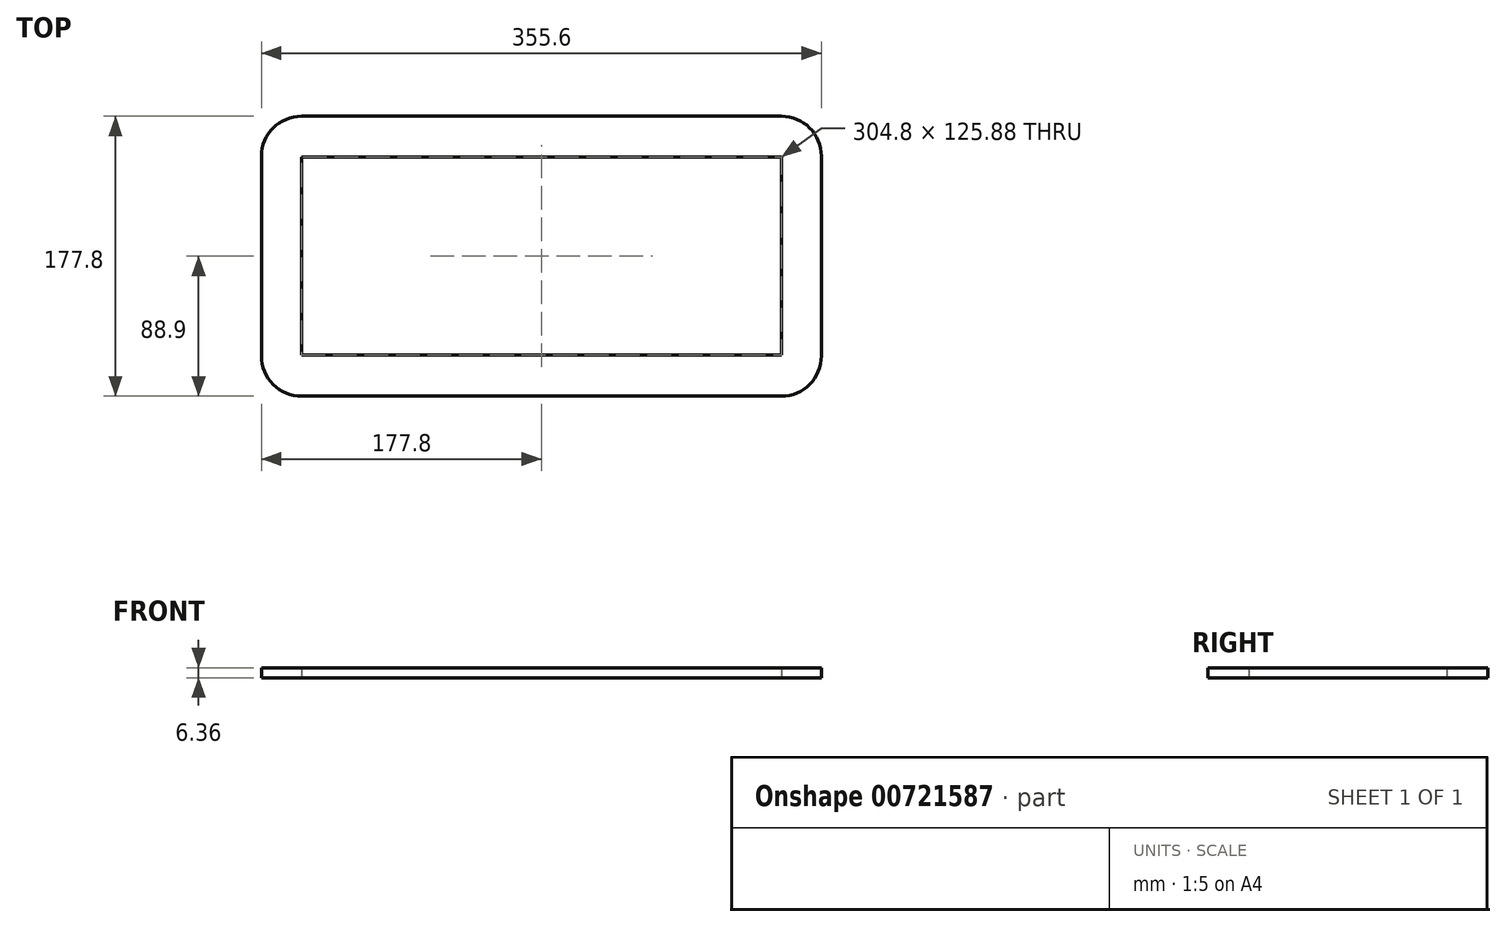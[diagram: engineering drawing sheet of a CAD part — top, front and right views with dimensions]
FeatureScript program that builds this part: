
annotation { "Feature Type Name" : "Feature", "Feature Type Description" : "" }
export const myFeature = defineFeature(function(context is Context, id is Id, definition is map)
    precondition{}
    {
        {
            var Q0;
            Q0=qCreatedBy(makeId("Top.planeOp"),FACE);
            var sketch = newSketch(context, id + "F0", { "sketchPlane" : qUnion([Q0])});
            skLineSegment(sketch, "E0.bottom", {"start": v(152.4, -62.94) * mm, "end": v(-152.4, -62.94) * mm});
            skLineSegment(sketch, "E0.top", {"start": v(152.4, 62.94) * mm, "end": v(-152.4, 62.94) * mm});
            skLineSegment(sketch, "E0.left", {"start": v(152.4, -62.94) * mm, "end": v(152.4, 62.94) * mm});
            skLineSegment(sketch, "E0.right", {"start": v(-152.4, -62.94) * mm, "end": v(-152.4, 62.94) * mm});
            skPoint(sketch, "E0.middle", {"position": v(0, 0) * mm});
            skSolve(sketch);
        }
        {
            var Q0;
            Q0=makeQuery(id+"F0.imprint","IMPRINT",FACE,{"disambiguationData":[TD([[makeQuery(id+"F0.imprint","IMPRINT",EDGE,{"derivedFrom":sQuery(id+"F0.wireOp",EDGE,"E0.bottom")}),-1.0]])]});
            extrude(context, id + "F1", {"entities" : qUnion([Q0]), "depth" : 6.35 * mm, "offsetDistance" : 25.4 * mm, "symmetric" : true});
        }
        {
            var Q0;
            Q0=qCreatedBy(makeId("Top.planeOp"),FACE);
            var sketch = newSketch(context, id + "F2", { "sketchPlane" : qUnion([Q0])});
            skLineSegment(sketch, "E1.bottom", {"start": v(177.8, -88.9) * mm, "end": v(-177.8, -88.9) * mm});
            skLineSegment(sketch, "E1.top", {"start": v(177.8, 88.9) * mm, "end": v(-177.8, 88.9) * mm});
            skLineSegment(sketch, "E1.left", {"start": v(177.8, -88.9) * mm, "end": v(177.8, 88.9) * mm});
            skLineSegment(sketch, "E1.right", {"start": v(-177.8, -88.9) * mm, "end": v(-177.8, 88.9) * mm});
            skPoint(sketch, "E1.middle", {"position": v(0, 0) * mm});
            skSolve(sketch);
        }
        {
            var Q0;
            Q0 = qSketchRegion(id + "F2", true);
            extrude(context, id + "F3", {"entities" : qUnion([Q0]), "operationType" : NewBodyOperationType.ADD, "depth" : 6.35 * mm, "offsetDistance" : 25.4 * mm, "symmetric" : true});
        }
        {
            var Q0;
            Q0 = qSketchRegion(id + "F0", true);
            extrude(context, id + "F4", {"entities" : qUnion([Q0]), "operationType" : NewBodyOperationType.REMOVE, "depth" : 25.4 * mm, "offsetDistance" : 25.4 * mm, "symmetric" : true});
        }
        {
            var Q0;
            Q0=makeQuery(id+"F3.opExtrude","SWEPT_EDGE",EDGE,{"disambiguationData":[OSD([sQuery(id+"F2.wireOp",EDGE,"E1.top"),sQuery(id+"F2.wireOp",EDGE,"E1.right")])]});
            fillet(context, id + "F5", {"entities" : qUnion([Q0]), "radius" : 25.4 * mm, "tangentPropagation" : true, "allowEdgeOverflow" : false});
        }
        {
            var Q0;
            Q0=makeQuery(id+"F3.opExtrude","SWEPT_EDGE",EDGE,{"disambiguationData":[OSD([sQuery(id+"F2.wireOp",EDGE,"E1.top"),sQuery(id+"F2.wireOp",EDGE,"E1.left")])]});
            fillet(context, id + "F6", {"entities" : qUnion([Q0]), "radius" : 25.4 * mm, "tangentPropagation" : true, "allowEdgeOverflow" : false});
        }
        {
            var Q0;
            Q0=makeQuery(id+"F3.opExtrude","SWEPT_EDGE",EDGE,{"disambiguationData":[OSD([sQuery(id+"F2.wireOp",EDGE,"E1.bottom"),sQuery(id+"F2.wireOp",EDGE,"E1.left")])]});
            fillet(context, id + "F7", {"entities" : qUnion([Q0]), "radius" : 25.4 * mm, "tangentPropagation" : true, "allowEdgeOverflow" : false});
        }
        {
            var Q0;
            Q0=makeQuery(id+"F3.opExtrude","SWEPT_EDGE",EDGE,{"disambiguationData":[OSD([sQuery(id+"F2.wireOp",EDGE,"E1.bottom"),sQuery(id+"F2.wireOp",EDGE,"E1.right")])]});
            fillet(context, id + "F8", {"entities" : qUnion([Q0]), "radius" : 25.4 * mm, "tangentPropagation" : true, "allowEdgeOverflow" : false});
        }
    });
